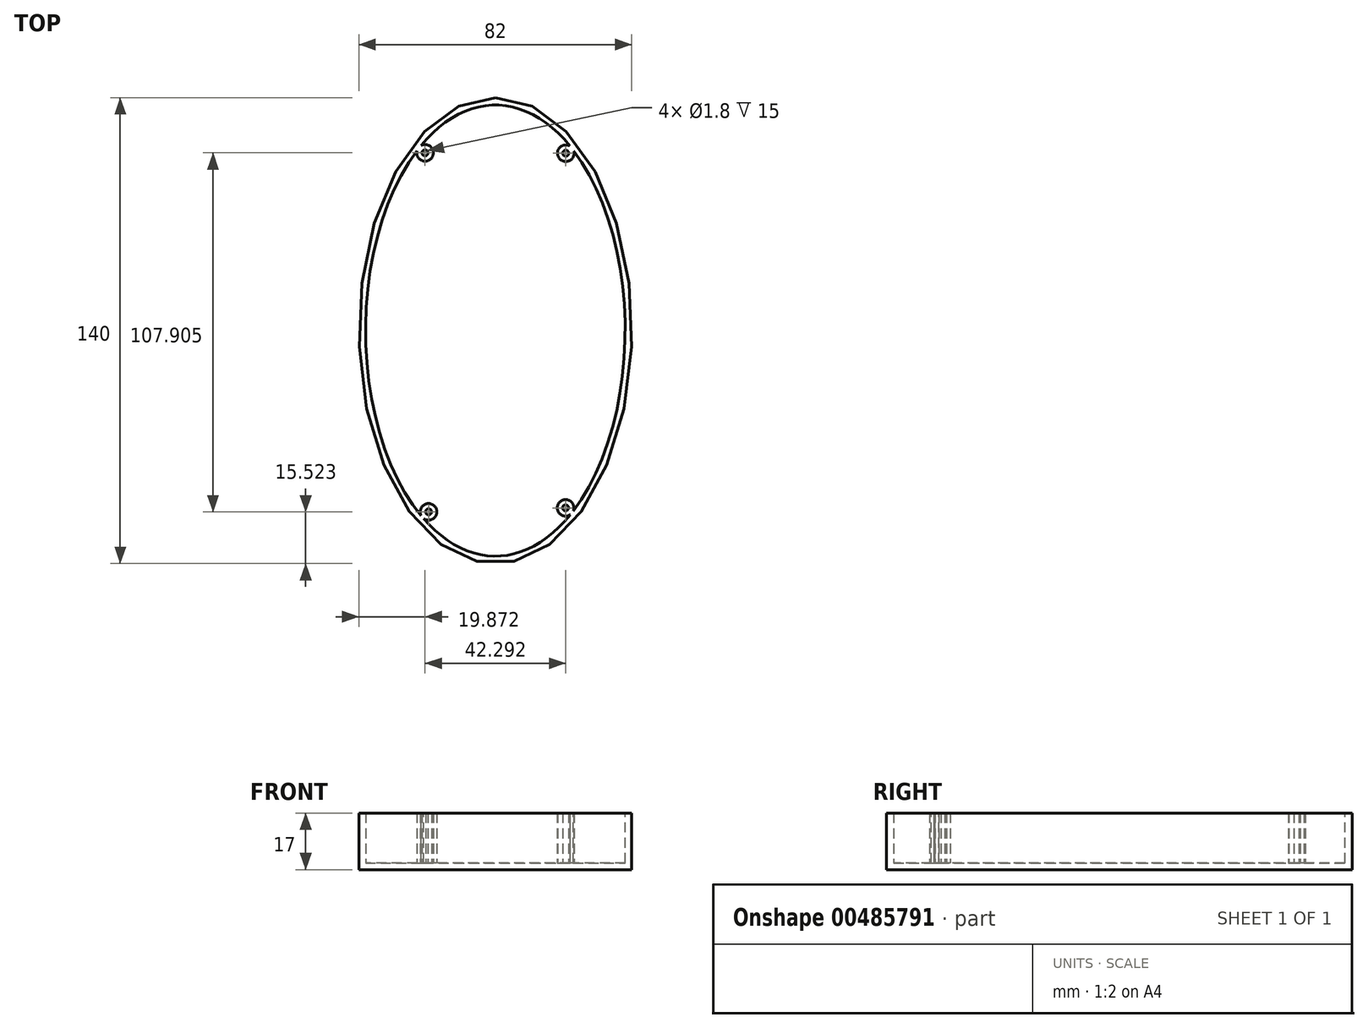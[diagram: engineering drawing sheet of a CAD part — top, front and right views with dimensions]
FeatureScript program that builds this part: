
annotation { "Feature Type Name" : "Feature", "Feature Type Description" : "" }
export const myFeature = defineFeature(function(context is Context, id is Id, definition is map)
    precondition{}
    {
        {
            var Q0;
            Q0=qCreatedBy(makeId("Top.planeOp"),FACE);
            var sketch = newSketch(context, id + "F0", { "sketchPlane" : qUnion([Q0])});
            skEllipse(sketch, "E0", {"center": v(-6.22, 3.26) * mm, "majorRadius": 70 * mm, "minorRadius": 41 * mm, "majorAxis": v(0, 1)});
            skSolve(sketch);
        }
        {
            var Q0;
            Q0=qSketchRegion(id+"F0",true);
            extrude(context, id + "F1", {"entities" : qUnion([Q0]), "depth" : 17 * mm});
        }
        {
            var Q0;
            Q0=makeQuery(id+"F1.opExtrude","CAP_FACE",FACE,{"disambiguationData":[OSD([sQuery(id+"F0.wireOp",EDGE,"E0")])],"isStart":false});
            var sketch = newSketch(context, id + "F2", { "sketchPlane" : qUnion([Q0])});
            skEllipse(sketch, "E1", {"center": v(-6.22, 3.26) * mm, "majorRadius": 67.8 * mm, "minorRadius": 39 * mm, "majorAxis": v(0, 1)});
            skSolve(sketch);
        }
        {
            var Q0;
            Q0=makeQuery(id+"F2.imprint","IMPRINT",FACE,{"disambiguationData":[TD([[makeQuery(id+"F2.imprint","IMPRINT",EDGE,{"derivedFrom":sQuery(id+"F2.wireOp",EDGE,"E1")}),1.0]])]});
            extrude(context, id + "F3", {"entities" : qUnion([Q0]), "operationType" : NewBodyOperationType.REMOVE, "oppositeDirection" : true, "depth" : 15 * mm});
        }
        {
            var Q0;
            Q0=makeQuery(id+"F3.boolean.opBoolean","COPY",FACE,{"derivedFrom":makeQuery(id+"F3.opExtrude","CAP_FACE",FACE,{"disambiguationData":[OSD([sQuery(id+"F2.wireOp",EDGE,"E1")])],"isStart":false})});
            var sketch = newSketch(context, id + "F4", { "sketchPlane" : qUnion([Q0])});
            skCircle(sketch, "E2", {"center": v(-27.35, 56.69) * mm, "radius": 2.5 * mm});
            skPoint(sketch, "E2.first.point", {"position": v(-28.49, 58.91) * mm});
            skPoint(sketch, "E2.second.point", {"position": v(-26.1, 54.53) * mm});
            skPoint(sketch, "E2.third.point", {"position": v(-27.44, 54.19) * mm});
            skCircle(sketch, "E3", {"center": v(-27.35, 56.69) * mm, "radius": 0.9 * mm});
            skSolve(sketch);
        }
        {
            var Q0;
            {var subQ0=sQuery(id+"F4.wireOp",EDGE,"E2");var subQ1=makeQuery(id+"F3.boolean.opBoolean","COPY",EDGE,{"derivedFrom":makeQuery(id+"F3.opExtrude","CAP_EDGE",EDGE,{"disambiguationData":[OSD([sQuery(id+"F2.wireOp",EDGE,"E1")])],"isStart":false})});var subQ2=makeQuery(id+"F4.imprint","INTERSECT",VERTEX,{"disambiguationData":[OD(0.0)],"derivedFrom":[subQ1,subQ0]});Q0=makeQuery(id+"F4.imprint","IMPRINT",FACE,{"disambiguationData":[TD([[makeQuery(id+"F4.imprint","IMPRINT",EDGE,{"disambiguationData":[TD([[subQ2,-1.0]])],"derivedFrom":subQ0}),1.0]])]});}
            extrude(context, id + "F5", {"entities" : qUnion([Q0]), "operationType" : NewBodyOperationType.ADD, "depth" : 15 * mm});
        }
        {
            var Q0;
            Q0=makeQuery(id+"F3.boolean.opBoolean","COPY",FACE,{"derivedFrom":makeQuery(id+"F3.opExtrude","CAP_FACE",FACE,{"disambiguationData":[OSD([sQuery(id+"F2.wireOp",EDGE,"E1")])],"isStart":false})});
            var sketch = newSketch(context, id + "F6", { "sketchPlane" : qUnion([Q0])});
            skCircle(sketch, "E4", {"center": v(14.94, 56.58) * mm, "radius": 2.5 * mm});
            skPoint(sketch, "E4.first.point", {"position": v(12.51, 56) * mm});
            skPoint(sketch, "E4.second.point", {"position": v(17.34, 57.29) * mm});
            skPoint(sketch, "E4.third.point", {"position": v(16.01, 54.32) * mm});
            skCircle(sketch, "E5", {"center": v(14.94, 56.58) * mm, "radius": 0.9 * mm});
            skSolve(sketch);
        }
        {
            var Q0;
            {var subQ0=sQuery(id+"F6.wireOp",EDGE,"E4");var subQ1=makeQuery(id+"F3.boolean.opBoolean","COPY",EDGE,{"derivedFrom":makeQuery(id+"F3.opExtrude","CAP_EDGE",EDGE,{"disambiguationData":[OSD([sQuery(id+"F2.wireOp",EDGE,"E1")])],"isStart":false})});var subQ2=makeQuery(id+"F6.imprint","INTERSECT",VERTEX,{"disambiguationData":[OD(0.0)],"derivedFrom":[subQ1,subQ0]});Q0=makeQuery(id+"F6.imprint","IMPRINT",FACE,{"disambiguationData":[TD([[makeQuery(id+"F6.imprint","IMPRINT",EDGE,{"disambiguationData":[TD([[subQ2,1.0]])],"derivedFrom":subQ0}),1.0]])]});}
            extrude(context, id + "F7", {"entities" : qUnion([Q0]), "operationType" : NewBodyOperationType.ADD, "depth" : 15 * mm});
        }
        {
            var Q0;
            Q0=makeQuery(id+"F3.boolean.opBoolean","COPY",FACE,{"derivedFrom":makeQuery(id+"F3.opExtrude","CAP_FACE",FACE,{"disambiguationData":[OSD([sQuery(id+"F2.wireOp",EDGE,"E1")])],"isStart":false})});
            var sketch = newSketch(context, id + "F8", { "sketchPlane" : qUnion([Q0])});
            skCircle(sketch, "E6", {"center": v(-26.28, -51.22) * mm, "radius": 2.5 * mm});
            skPoint(sketch, "E6.first.point", {"position": v(-28.49, -50.03) * mm});
            skPoint(sketch, "E6.second.point", {"position": v(-24.98, -49.08) * mm});
            skPoint(sketch, "E6.third.point", {"position": v(-28.49, -52.4) * mm});
            skCircle(sketch, "E7", {"center": v(-26.28, -51.22) * mm, "radius": 0.9 * mm});
            skSolve(sketch);
        }
        {
            var Q0;
            {var subQ0=sQuery(id+"F8.wireOp",EDGE,"E6");var subQ1=makeQuery(id+"F7.boolean.opBoolean","SPLIT",EDGE,{"disambiguationData":[OD(0.0)],"derivedFrom":makeQuery(id+"F3.boolean.opBoolean","COPY",EDGE,{"derivedFrom":makeQuery(id+"F3.opExtrude","CAP_EDGE",EDGE,{"disambiguationData":[OSD([sQuery(id+"F2.wireOp",EDGE,"E1")])],"isStart":false})})});var subQ2=makeQuery(id+"F8.imprint","INTERSECT",VERTEX,{"disambiguationData":[OD(0.0)],"derivedFrom":[subQ1,subQ0]});Q0=makeQuery(id+"F8.imprint","IMPRINT",FACE,{"disambiguationData":[TD([[makeQuery(id+"F8.imprint","IMPRINT",EDGE,{"disambiguationData":[TD([[subQ2,1.0]])],"derivedFrom":subQ0}),1.0]])]});}
            extrude(context, id + "F9", {"entities" : qUnion([Q0]), "operationType" : NewBodyOperationType.ADD, "depth" : 15 * mm});
        }
        {
            var Q0;
            Q0=makeQuery(id+"F3.boolean.opBoolean","COPY",FACE,{"derivedFrom":makeQuery(id+"F3.opExtrude","CAP_FACE",FACE,{"disambiguationData":[OSD([sQuery(id+"F2.wireOp",EDGE,"E1")])],"isStart":false})});
            var sketch = newSketch(context, id + "F10", { "sketchPlane" : qUnion([Q0])});
            skCircle(sketch, "E8", {"center": v(14.89, -50.02) * mm, "radius": 2.5 * mm});
            skPoint(sketch, "E8.first.point", {"position": v(17.2, -50.95) * mm});
            skPoint(sketch, "E8.second.point", {"position": v(12.45, -49.45) * mm});
            skPoint(sketch, "E8.third.point", {"position": v(13.95, -47.7) * mm});
            skCircle(sketch, "E9", {"center": v(14.89, -50.02) * mm, "radius": 0.9 * mm});
            skSolve(sketch);
        }
        {
            var Q0;
            {var subQ0=sQuery(id+"F10.wireOp",EDGE,"E8");var subQ1=sQuery(id+"F2.wireOp",EDGE,"E1");var subQ2=makeQuery(id+"F9.boolean.opBoolean","SPLIT",EDGE,{"disambiguationData":[TD([makeQuery(id+"F7.opExtrude","SWEPT_FACE",FACE,{"disambiguationData":[OSD([sQuery(id+"F6.wireOp",EDGE,"E4")])]})])],"derivedFrom":makeQuery(id+"F7.boolean.opBoolean","SPLIT",EDGE,{"disambiguationData":[OD(0.0)],"derivedFrom":makeQuery(id+"F3.boolean.opBoolean","COPY",EDGE,{"derivedFrom":makeQuery(id+"F3.opExtrude","CAP_EDGE",EDGE,{"disambiguationData":[OSD([subQ1])],"isStart":false})})})});var subQ3=makeQuery(id+"F10.imprint","INTERSECT",VERTEX,{"disambiguationData":[OD(0.0)],"derivedFrom":[subQ2,subQ0]});Q0=makeQuery(id+"F10.imprint","IMPRINT",FACE,{"disambiguationData":[TD([[makeQuery(id+"F10.imprint","IMPRINT",EDGE,{"disambiguationData":[TD([[subQ3,-1.0]])],"derivedFrom":subQ0}),1.0]])]});}
            extrude(context, id + "F11", {"entities" : qUnion([Q0]), "operationType" : NewBodyOperationType.ADD, "depth" : 15 * mm});
        }
        {
            var Q0;
            {var subQ0=sQuery(id+"F2.wireOp",EDGE,"E1");Q0=makeQuery(id+"F11.boolean.opBoolean","MERGE",FACE,{"derivedFrom":[makeQuery(id+"F9.boolean.opBoolean","MERGE",FACE,{"derivedFrom":[makeQuery(id+"F7.boolean.opBoolean","MERGE",FACE,{"derivedFrom":[makeQuery(id+"F5.boolean.opBoolean","MERGE",FACE,{"derivedFrom":[makeQuery(id+"F1.opExtrude","CAP_FACE",FACE,{"disambiguationData":[OSD([sQuery(id+"F0.wireOp",EDGE,"E0")])],"isStart":false}),makeQuery(id+"F5.opExtrude","CAP_FACE",FACE,{"disambiguationData":[OSD([subQ0,sQuery(id+"F4.wireOp",EDGE,"E2")])],"isStart":false})]}),makeQuery(id+"F7.opExtrude","CAP_FACE",FACE,{"disambiguationData":[OSD([subQ0,sQuery(id+"F6.wireOp",EDGE,"E4")])],"isStart":false})]}),makeQuery(id+"F9.opExtrude","CAP_FACE",FACE,{"disambiguationData":[OSD([subQ0,sQuery(id+"F8.wireOp",EDGE,"E6")])],"isStart":false})]}),makeQuery(id+"F11.opExtrude","CAP_FACE",FACE,{"disambiguationData":[OSD([subQ0,sQuery(id+"F10.wireOp",EDGE,"E8")])],"isStart":false})]});}
            var sketch = newSketch(context, id + "F12", { "sketchPlane" : qUnion([Q0])});
            skSolve(sketch);
        }
        {
            var Q0;
            {var subQ8=sQuery(id+"F0.wireOp",EDGE,"E0");Q0=makeQuery(id+"F12.imprint","IMPRINT",FACE,{"disambiguationData":[TD([[makeQuery(id+"F12.imprint","IMPRINT",EDGE,{"derivedFrom":makeQuery(id+"F1.opExtrude","CAP_EDGE",EDGE,{"disambiguationData":[OSD([subQ8])],"isStart":false})}),1.0]])]});}
            var sketch = newSketch(context, id + "F13", { "sketchPlane" : qUnion([Q0])});
            skCircle(sketch, "E10.0", {"center": v(-27.35, 56.69) * mm, "radius": 0.9 * mm});
            skCircle(sketch, "E11.0", {"center": v(14.94, 56.58) * mm, "radius": 0.9 * mm});
            skCircle(sketch, "E12.0", {"center": v(-26.28, -51.22) * mm, "radius": 0.9 * mm});
            skCircle(sketch, "E13.0", {"center": v(14.89, -50.02) * mm, "radius": 0.9 * mm});
            skSolve(sketch);
        }
        {
            var Q0;
            Q0=qSketchRegion(id+"F13",true);
            extrude(context, id + "F14", {"entities" : qUnion([Q0]), "operationType" : NewBodyOperationType.REMOVE, "oppositeDirection" : true, "depth" : 9 * mm});
        }
    });
